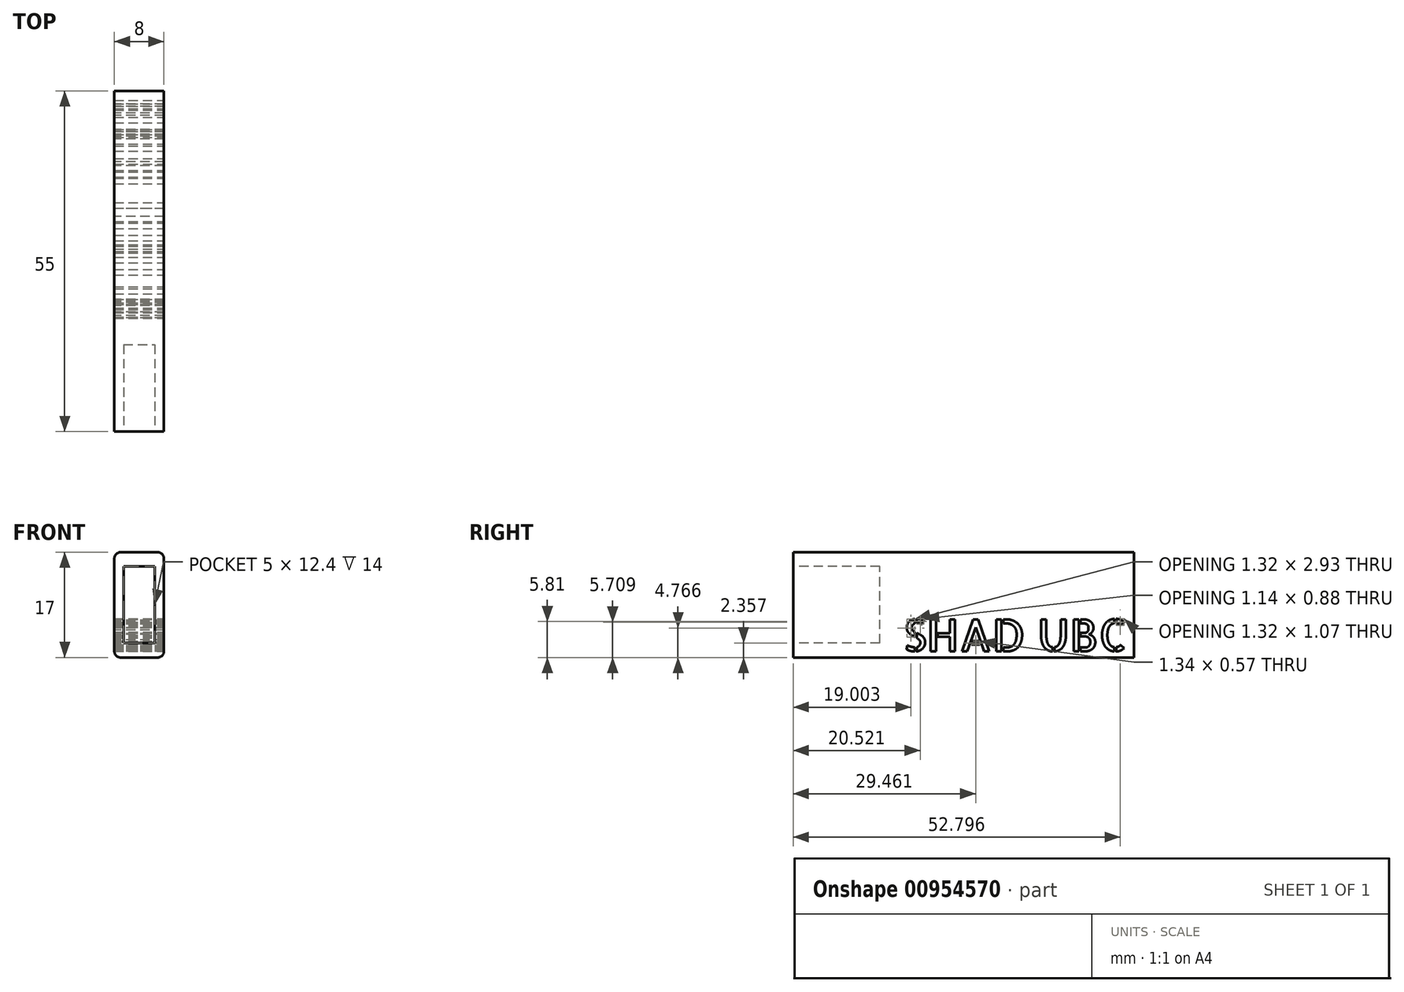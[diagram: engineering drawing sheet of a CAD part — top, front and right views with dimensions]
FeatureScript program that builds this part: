
annotation { "Feature Type Name" : "Feature", "Feature Type Description" : "" }
export const myFeature = defineFeature(function(context is Context, id is Id, definition is map)
    precondition{}
    {
        {
            var Q0;
            Q0=qCreatedBy(makeId("Front.planeOp"),FACE);
            var sketch = newSketch(context, id + "F0", { "sketchPlane" : qUnion([Q0])});
            skLineSegment(sketch, "E0.bottom", {"start": v(-7.5, 4) * mm, "end": v(7.5, 4) * mm});
            skLineSegment(sketch, "E0.top", {"start": v(-7.5, -4) * mm, "end": v(7.5, -4) * mm});
            skLineSegment(sketch, "E0.left", {"start": v(-8.5, 3) * mm, "end": v(-8.5, -3) * mm});
            skLineSegment(sketch, "E0.right", {"start": v(8.5, 3) * mm, "end": v(8.5, -3) * mm});
            skPoint(sketch, "E1.visualSharp", {"position": v(-8.5, 4) * mm});
            skArc(sketch, "E1.filletArc", {"start": v(-7.5, 4) * mm, "mid": v(-8.2, 3.7) * mm, "end": v(-8.5, 3) * mm});
            skPoint(sketch, "E2.visualSharp", {"position": v(-8.5, -4) * mm});
            skArc(sketch, "E2.filletArc", {"start": v(-8.5, -3) * mm, "mid": v(-8.2, -3.7) * mm, "end": v(-7.5, -4) * mm});
            skPoint(sketch, "E3.visualSharp", {"position": v(8.5, -4) * mm});
            skArc(sketch, "E3.filletArc", {"start": v(7.5, -4) * mm, "mid": v(8.2, -3.7) * mm, "end": v(8.5, -3) * mm});
            skPoint(sketch, "E4.visualSharp", {"position": v(8.5, 4) * mm});
            skArc(sketch, "E4.filletArc", {"start": v(8.5, 3) * mm, "mid": v(8.2, 3.7) * mm, "end": v(7.5, 4) * mm});
            skSolve(sketch);
        }
        {
            var Q0;
            Q0 = qSketchRegion(id + "F0", true);
            extrude(context, id + "F1", {"entities" : qUnion([Q0]), "depth" : 55 * mm, "offsetDistance" : 25 * mm});
        }
        {
            var Q0;
            Q0=makeQuery(id+"F1.opExtrude","CAP_FACE",FACE,{"disambiguationData":[OSD([sQuery(id+"F0.wireOp",EDGE,"E0.bottom"),sQuery(id+"F0.wireOp",EDGE,"E0.top"),sQuery(id+"F0.wireOp",EDGE,"E0.left"),sQuery(id+"F0.wireOp",EDGE,"E0.right"),sQuery(id+"F0.wireOp",EDGE,"E1.filletArc"),sQuery(id+"F0.wireOp",EDGE,"E2.filletArc"),sQuery(id+"F0.wireOp",EDGE,"E3.filletArc"),sQuery(id+"F0.wireOp",EDGE,"E4.filletArc")])],"isStart":false});
            var sketch = newSketch(context, id + "F2", { "sketchPlane" : qUnion([Q0])});
            skLineSegment(sketch, "E5.bottom", {"start": v(-6.2, 2.5) * mm, "end": v(6.2, 2.5) * mm});
            skLineSegment(sketch, "E5.top", {"start": v(-6.2, -2.5) * mm, "end": v(6.2, -2.5) * mm});
            skLineSegment(sketch, "E5.left", {"start": v(-6.2, 2.5) * mm, "end": v(-6.2, -2.5) * mm});
            skLineSegment(sketch, "E5.right", {"start": v(6.2, 2.5) * mm, "end": v(6.2, -2.5) * mm});
            skSolve(sketch);
        }
        {
            var Q0;
            Q0 = qSketchRegion(id + "F2", true);
            extrude(context, id + "F3", {"entities" : qUnion([Q0]), "operationType" : NewBodyOperationType.REMOVE, "oppositeDirection" : true, "depth" : 14 * mm, "offsetDistance" : 25 * mm});
        }
        {
            var Q0;
            Q0=makeQuery(id+"F1.opExtrude","SWEPT_BODY",BODY,{"disambiguationData":[OSD([sQuery(id+"F0.wireOp",EDGE,"E0.bottom"),sQuery(id+"F0.wireOp",EDGE,"E0.top"),sQuery(id+"F0.wireOp",EDGE,"E0.left"),sQuery(id+"F0.wireOp",EDGE,"E0.right"),sQuery(id+"F0.wireOp",EDGE,"E1.filletArc"),sQuery(id+"F0.wireOp",EDGE,"E2.filletArc"),sQuery(id+"F0.wireOp",EDGE,"E3.filletArc"),sQuery(id+"F0.wireOp",EDGE,"E4.filletArc")])]});
            var Q1;
            Q1=makeQuery(id+"F1.opExtrude","CAP_EDGE",EDGE,{"disambiguationData":[OSD([sQuery(id+"F0.wireOp",EDGE,"E1.filletArc")])],"isStart":true});
            transform(context, id + "F4", {"entities" : qUnion([Q0]), "transformType" : TransformType.ROTATION, "transformAxis" : qUnion([Q1]), "angle" : 90 * degree, "makeCopy" : false});
        }
        {
            var Q0;
            Q0=makeQuery(id+"F1.opExtrude","SWEPT_FACE",FACE,{"disambiguationData":[OSD([sQuery(id+"F0.wireOp",EDGE,"E0.top")])]});
            var sketch = newSketch(context, id + "F5", { "sketchPlane" : qUnion([Q0])});
            skText(sketch, "E6", { "text": "SHAD UBC", "fontName": "AllertaStencil-Regular.ttf"});
            const initialGuessF5  = {"E6": [-0.03726, 0.003, 1, 0, 0.00517]};
            skSetInitialGuess(sketch, initialGuessF5);
            skSolve(sketch);
        }
        {
            var Q0;
            Q0 = qSketchRegion(id + "F5", true);
            extrude(context, id + "F6", {"entities" : qUnion([Q0]), "operationType" : NewBodyOperationType.REMOVE, "oppositeDirection" : true, "depth" : 55 * mm, "offsetDistance" : 25 * mm});
        }
    });
